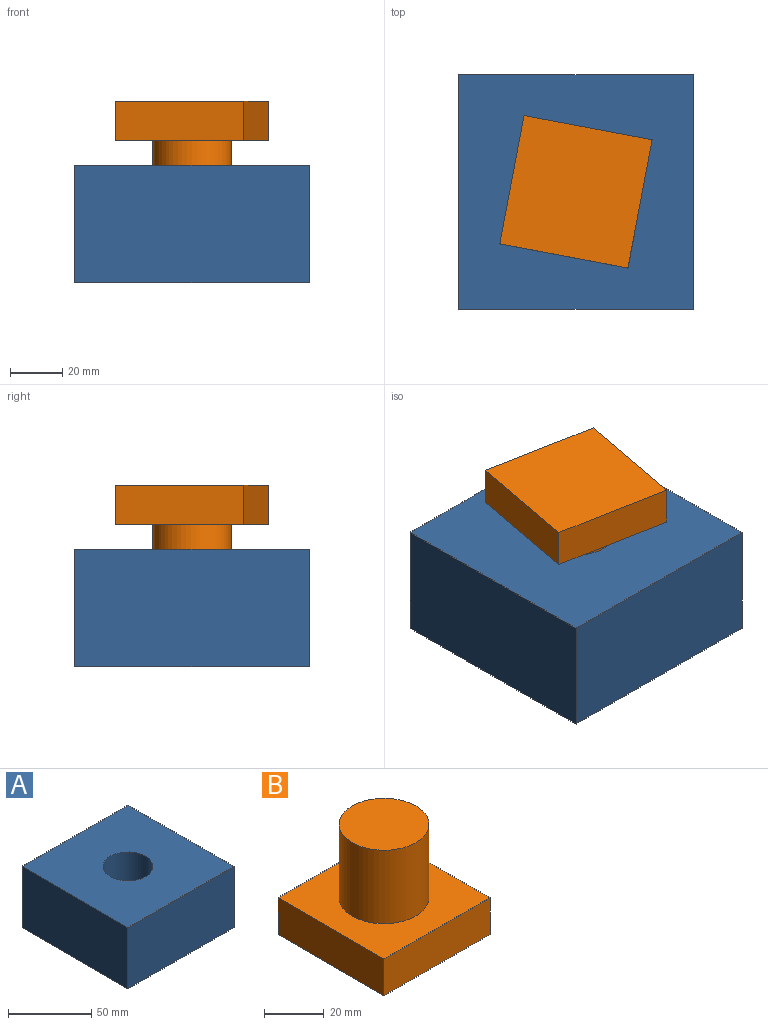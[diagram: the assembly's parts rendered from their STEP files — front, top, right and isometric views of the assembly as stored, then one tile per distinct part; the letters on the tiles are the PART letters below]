
ASSEMBLY  parts=2 mates=1
PART A: 8 faces, bbox 90x90x45 mm
  f0: plane 90x45mm, normal (0,-1,0), area 4050mm2, adj f1,f3,f4,f5
  f1: plane 90x45mm, normal (1,0,0), area 4050mm2, adj f0,f2,f4,f5
  f2: plane 90x45mm, normal (0,1,0), area 4050mm2, adj f1,f3,f4,f5
  f3: plane 90x45mm, normal (-1,0,0), area 4050mm2, adj f0,f2,f4,f5
  f4: plane 90x90mm, normal (0,0,1), area 7393.1mm2, adj f0,f1,f2,f3,f6
  f5: plane 90x90mm, normal (0,0,-1), area 8100mm2, adj f0,f1,f2,f3
  f6: cylinder r=15mm len=30mm, axis (0,0,1), area 2827.4mm2, adj f4,f7
  f7: plane 30x30mm, normal (0,0,1), area 706.9mm2, adj f6
PART B: 8 faces, bbox 50x50x45 mm
  f0: plane 50x15mm, normal (0,-1,0), area 750mm2, adj f1,f3,f4,f5
  f1: plane 50x15mm, normal (1,0,0), area 750mm2, adj f0,f2,f4,f5
  f2: plane 50x15mm, normal (0,1,0), area 750mm2, adj f1,f3,f4,f5
  f3: plane 50x15mm, normal (-1,0,0), area 750mm2, adj f0,f2,f4,f5
  f4: plane 50x50mm, normal (0,0,1), area 1793.1mm2, adj f0,f1,f2,f3,f6
  f5: plane 50x50mm, normal (0,0,-1), area 2500mm2, adj f0,f1,f2,f3
  f6: cylinder r=15mm len=30mm, axis (0,0,-1), area 2827.4mm2, adj f4,f7
  f7: plane 30x30mm, normal (0,0,1), area 706.9mm2, adj f6
PLACE A at identity fixed
PLACE B rot(axis=(0.77,0.64,0),180deg) t=(0,0,69.49)mm
MATE cylindrical A.f6 <-> B.f6  axis (0,0,1) through (0,0,45)mm
